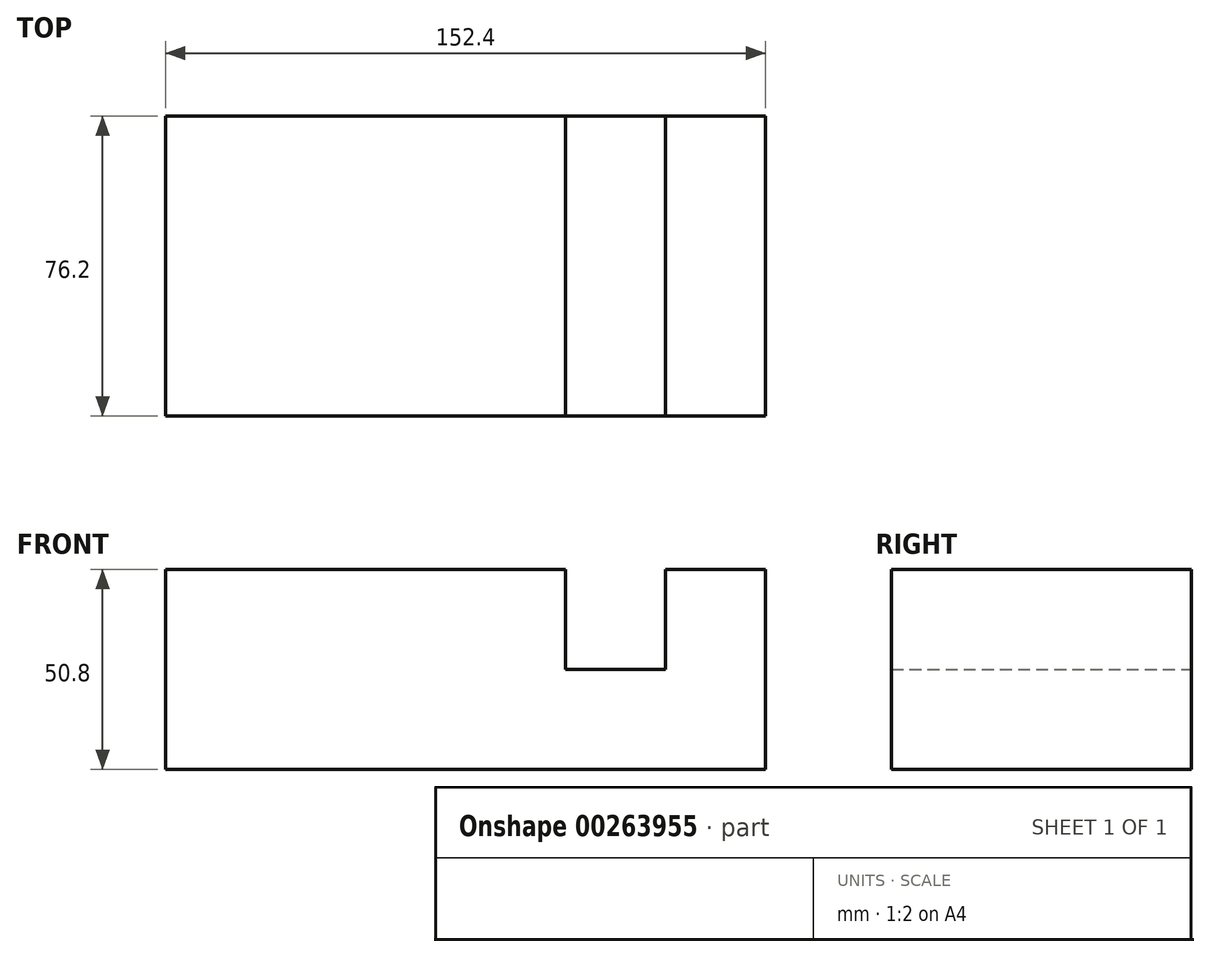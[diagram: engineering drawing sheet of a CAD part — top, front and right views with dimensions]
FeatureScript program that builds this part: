
annotation { "Feature Type Name" : "Feature", "Feature Type Description" : "" }
export const myFeature = defineFeature(function(context is Context, id is Id, definition is map)
    precondition{}
    {
        {
            var Q0;
            Q0=qCreatedBy(makeId("Front.planeOp"),FACE);
            var sketch = newSketch(context, id + "F0", { "sketchPlane" : qUnion([Q0])});
            skLineSegment(sketch, "E0.bottom", {"start": v(-74.05, 0) * mm, "end": v(27.55, 0) * mm});
            skLineSegment(sketch, "E0.top", {"start": v(-74.05, -50.8) * mm, "end": v(78.35, -50.8) * mm});
            skLineSegment(sketch, "E0.left", {"start": v(-74.05, 0) * mm, "end": v(-74.05, -50.8) * mm});
            skLineSegment(sketch, "E0.right", {"start": v(78.35, 0) * mm, "end": v(78.35, -50.8) * mm});
            skLineSegment(sketch, "E1", {"start": v(78.35, 0) * mm, "end": v(52.95, 0) * mm});
            skLineSegment(sketch, "E2", {"start": v(78.35, 0) * mm, "end": v(78.35, -25.4) * mm});
            skLineSegment(sketch, "E3", {"start": v(52.95, -25.4) * mm, "end": v(52.95, 0) * mm});
            skLineSegment(sketch, "E4", {"start": v(52.95, -25.4) * mm, "end": v(27.55, -25.4) * mm});
            skLineSegment(sketch, "E5", {"start": v(27.55, -25.4) * mm, "end": v(27.55, 0) * mm});
            skLineSegment(sketch, "E6.trimOffspring", {"start": v(52.95, 0) * mm, "end": v(78.35, 0) * mm});
            skSolve(sketch);
        }
        {
            var Q0;
            Q0=makeQuery(id+"F0.imprint","IMPRINT",FACE,{"disambiguationData":[TD([[makeQuery(id+"F0.imprint","IMPRINT",EDGE,{"derivedFrom":sQuery(id+"F0.wireOp",EDGE,"E0.bottom")}),-1.0]])]});
            extrude(context, id + "F1", {"entities" : qUnion([Q0]), "depth" : 76.2 * mm});
        }
    });
